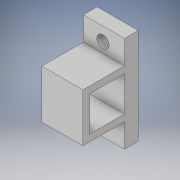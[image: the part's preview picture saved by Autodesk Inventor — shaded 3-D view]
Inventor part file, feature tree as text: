
AUTODESK INVENTOR PART (.ipt)
format: ipt  version: 2019.3 (Build 233278000, 278)  size: 117,248 bytes
history: native  units: mm
features: reference x13, other x6, sketch x2, extrude x2, plane x1
ambient origin geometry x8: Origin, YZ Plane, XZ Plane, XY Plane, X Axis, Y Axis, Z Axis, Center Point
bodies: Solid1 (feature_tree)
feature tree (24):
  sketch  "Sketch1"  dims[d0=10.0mm d1=0.0mm d2=10.0mm d3=0.0mm]
  plane  "Work Plane1"
  extrude  "Extrusion1"  Depth=10.0mm TaperAngle=0.0deg
  extrude  "Extrusion2"  [1 undecoded]
  reference  "Reference1"
  reference  "Reference2"
  reference  "Reference3"
  reference  "Reference4"
  reference  "Reference5"
  reference  "Reference6"
  reference  "Reference7"
  sketch  "Sketch2"
  reference  "Reference8"
  reference  "Reference9"
  reference  "Reference10"
  reference  "Reference11"
  reference  "Reference12"
  reference  "Reference13"
  parser-record x1  (decoder bookkeeping rows leaked as tree rows — omitted from the tree; the rows remain in map.json)
  other  "Assembly.iam"
  other  "CameraBracket:1"
  other  "RailMount:1"
  other  "CornerBracket:2"
  other  "LateralBars:1"
note: 1 required parameter value undecoded (feature->parameter linkage not recoverable at this tier; creation-order binding heuristic only, values carry confidence <= 0.55)
note: 1 file-system path scrubbed to <path> (originals preserved in map.json)
